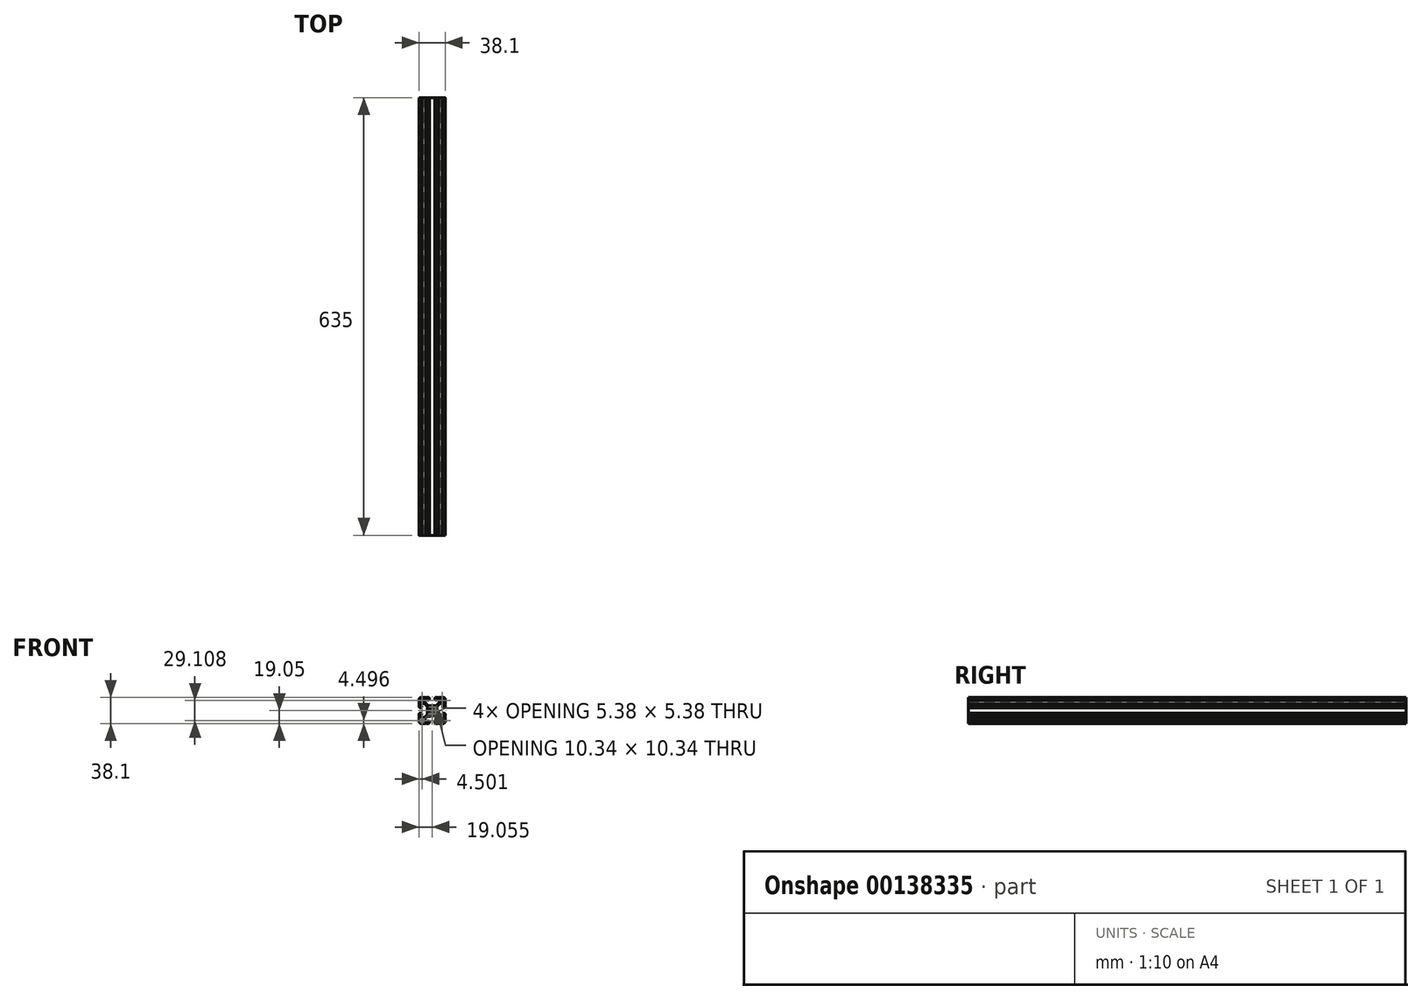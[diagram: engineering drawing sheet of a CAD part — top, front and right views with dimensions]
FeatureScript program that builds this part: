
annotation { "Feature Type Name" : "Feature", "Feature Type Description" : "" }
export const myFeature = defineFeature(function(context is Context, id is Id, definition is map)
    precondition{}
    {
        {
            var Q0;
            Q0=qCreatedBy(makeId("Front.planeOp"),FACE);
            var sketch = newSketch(context, id + "F0", { "sketchPlane" : qUnion([Q0])});
            skLineSegment(sketch, "E0", {"start": v(-126.4, 59.55) * mm, "end": v(-126.4, 54.72) * mm});
            skArc(sketch, "E1", {"start": v(-126.4, 53.2) * mm, "mid": v(-125.63, 53.96) * mm, "end": v(-126.4, 54.72) * mm});
            skArc(sketch, "E2", {"start": v(-126.4, 53.2) * mm, "mid": v(-125.47, 50.93) * mm, "end": v(-123.2, 50) * mm});
            skArc(sketch, "E3", {"start": v(-121.67, 50) * mm, "mid": v(-122.43, 50.76) * mm, "end": v(-123.2, 50) * mm});
            skLineSegment(sketch, "E4", {"start": v(-121.67, 50) * mm, "end": v(-116.84, 50) * mm});
            skArc(sketch, "E5", {"start": v(-115.32, 50) * mm, "mid": v(-116.08, 50.76) * mm, "end": v(-116.84, 50) * mm});
            skLineSegment(sketch, "E6", {"start": v(-115.32, 50) * mm, "end": v(-112.98, 50) * mm});
            skArc(sketch, "E7", {"start": v(-112.98, 50) * mm, "mid": v(-111.87, 50.46) * mm, "end": v(-111.4, 51.57) * mm});
            skLineSegment(sketch, "E8", {"start": v(-111.4, 51.57) * mm, "end": v(-111.4, 52.49) * mm});
            skArc(sketch, "E9", {"start": v(-111.4, 52.49) * mm, "mid": v(-111.87, 53.6) * mm, "end": v(-112.98, 54.06) * mm});
            skLineSegment(sketch, "E10", {"start": v(-112.98, 54.06) * mm, "end": v(-113.7, 54.06) * mm});
            skArc(sketch, "E11", {"start": v(-113.7, 54.06) * mm, "mid": v(-113.96, 53.95) * mm, "end": v(-114.08, 53.68) * mm});
            skLineSegment(sketch, "E12", {"start": v(-114.08, 53.68) * mm, "end": v(-114.08, 53.35) * mm});
            skArc(sketch, "E13", {"start": v(-114.46, 52.97) * mm, "mid": v(-114.19, 53.08) * mm, "end": v(-114.08, 53.35) * mm});
            skLineSegment(sketch, "E14", {"start": v(-114.46, 52.97) * mm, "end": v(-116.74, 52.97) * mm});
            skArc(sketch, "E15", {"start": v(-117.63, 53.86) * mm, "mid": v(-117.37, 53.23) * mm, "end": v(-116.74, 52.97) * mm});
            skLineSegment(sketch, "E16", {"start": v(-117.63, 53.86) * mm, "end": v(-117.63, 56.67) * mm});
            skArc(sketch, "E17", {"start": v(-117.26, 57.57) * mm, "mid": v(-117.54, 57.16) * mm, "end": v(-117.63, 56.67) * mm});
            skLineSegment(sketch, "E18", {"start": v(-117.26, 57.57) * mm, "end": v(-112.9, 61.93) * mm});
            skArc(sketch, "E19", {"start": v(-112, 62.3) * mm, "mid": v(-112.49, 62.2) * mm, "end": v(-112.9, 61.93) * mm});
            skLineSegment(sketch, "E20", {"start": v(-112, 62.3) * mm, "end": v(-102.7, 62.3) * mm});
            skArc(sketch, "E21", {"start": v(-101.8, 61.93) * mm, "mid": v(-102.2, 62.2) * mm, "end": v(-102.7, 62.3) * mm});
            skLineSegment(sketch, "E22", {"start": v(-101.8, 61.93) * mm, "end": v(-97.43, 57.57) * mm});
            skArc(sketch, "E23", {"start": v(-97.06, 56.67) * mm, "mid": v(-97.15, 57.16) * mm, "end": v(-97.43, 57.57) * mm});
            skLineSegment(sketch, "E24", {"start": v(-97.06, 56.67) * mm, "end": v(-97.06, 53.86) * mm});
            skArc(sketch, "E25", {"start": v(-97.95, 52.97) * mm, "mid": v(-97.32, 53.23) * mm, "end": v(-97.06, 53.86) * mm});
            skLineSegment(sketch, "E26", {"start": v(-97.95, 52.97) * mm, "end": v(-100.23, 52.97) * mm});
            skArc(sketch, "E27", {"start": v(-100.61, 53.35) * mm, "mid": v(-100.5, 53.08) * mm, "end": v(-100.23, 52.97) * mm});
            skLineSegment(sketch, "E28", {"start": v(-100.61, 53.35) * mm, "end": v(-100.61, 53.68) * mm});
            skArc(sketch, "E29", {"start": v(-100.61, 53.68) * mm, "mid": v(-100.73, 53.95) * mm, "end": v(-101, 54.06) * mm});
            skLineSegment(sketch, "E30", {"start": v(-101, 54.06) * mm, "end": v(-101.7, 54.06) * mm});
            skArc(sketch, "E31", {"start": v(-101.7, 54.06) * mm, "mid": v(-102.82, 53.6) * mm, "end": v(-103.28, 52.49) * mm});
            skLineSegment(sketch, "E32", {"start": v(-103.28, 52.49) * mm, "end": v(-103.28, 51.57) * mm});
            skArc(sketch, "E33", {"start": v(-103.28, 51.57) * mm, "mid": v(-102.82, 50.46) * mm, "end": v(-101.7, 50) * mm});
            skLineSegment(sketch, "E34", {"start": v(-101.7, 50) * mm, "end": v(-99.37, 50) * mm});
            skArc(sketch, "E35", {"start": v(-97.85, 50) * mm, "mid": v(-98.6, 50.76) * mm, "end": v(-99.37, 50) * mm});
            skLineSegment(sketch, "E36", {"start": v(-97.85, 50) * mm, "end": v(-93.02, 50) * mm});
            skArc(sketch, "E37", {"start": v(-91.5, 50) * mm, "mid": v(-92.26, 50.76) * mm, "end": v(-93.02, 50) * mm});
            skArc(sketch, "E38", {"start": v(-91.5, 50) * mm, "mid": v(-89.23, 50.93) * mm, "end": v(-88.3, 53.2) * mm});
            skArc(sketch, "E39", {"start": v(-88.3, 54.72) * mm, "mid": v(-89.06, 53.96) * mm, "end": v(-88.3, 53.2) * mm});
            skLineSegment(sketch, "E40", {"start": v(-88.3, 54.72) * mm, "end": v(-88.3, 59.55) * mm});
            skArc(sketch, "E41", {"start": v(-88.3, 61.07) * mm, "mid": v(-89.06, 60.31) * mm, "end": v(-88.3, 59.55) * mm});
            skLineSegment(sketch, "E42", {"start": v(-88.3, 61.07) * mm, "end": v(-88.3, 63.41) * mm});
            skArc(sketch, "E43", {"start": v(-88.3, 63.41) * mm, "mid": v(-88.76, 64.52) * mm, "end": v(-89.87, 64.99) * mm});
            skLineSegment(sketch, "E44", {"start": v(-89.87, 64.99) * mm, "end": v(-90.78, 64.99) * mm});
            skArc(sketch, "E45", {"start": v(-90.78, 64.99) * mm, "mid": v(-91.9, 64.52) * mm, "end": v(-92.36, 63.41) * mm});
            skLineSegment(sketch, "E46", {"start": v(-92.36, 63.41) * mm, "end": v(-92.36, 62.7) * mm});
            skArc(sketch, "E47", {"start": v(-92.36, 62.7) * mm, "mid": v(-92.25, 62.43) * mm, "end": v(-91.98, 62.32) * mm});
            skLineSegment(sketch, "E48", {"start": v(-91.98, 62.32) * mm, "end": v(-91.65, 62.32) * mm});
            skArc(sketch, "E49", {"start": v(-91.27, 61.94) * mm, "mid": v(-91.38, 62.2) * mm, "end": v(-91.65, 62.32) * mm});
            skLineSegment(sketch, "E50", {"start": v(-91.27, 61.94) * mm, "end": v(-91.27, 59.65) * mm});
            skArc(sketch, "E51", {"start": v(-92.16, 58.76) * mm, "mid": v(-91.53, 59.02) * mm, "end": v(-91.27, 59.65) * mm});
            skLineSegment(sketch, "E52", {"start": v(-92.16, 58.76) * mm, "end": v(-94.97, 58.76) * mm});
            skArc(sketch, "E53", {"start": v(-95.87, 59.13) * mm, "mid": v(-95.46, 58.86) * mm, "end": v(-94.97, 58.76) * mm});
            skLineSegment(sketch, "E54", {"start": v(-95.87, 59.13) * mm, "end": v(-100.23, 63.5) * mm});
            skArc(sketch, "E55", {"start": v(-100.6, 64.4) * mm, "mid": v(-100.5, 63.9) * mm, "end": v(-100.23, 63.5) * mm});
            skLineSegment(sketch, "E56", {"start": v(-100.6, 64.4) * mm, "end": v(-100.6, 73.7) * mm});
            skArc(sketch, "E57", {"start": v(-100.23, 74.6) * mm, "mid": v(-100.5, 74.2) * mm, "end": v(-100.6, 73.7) * mm});
            skLineSegment(sketch, "E58", {"start": v(-100.23, 74.6) * mm, "end": v(-95.87, 78.96) * mm});
            skArc(sketch, "E59", {"start": v(-94.97, 79.34) * mm, "mid": v(-95.46, 79.24) * mm, "end": v(-95.87, 78.96) * mm});
            skLineSegment(sketch, "E60", {"start": v(-94.97, 79.34) * mm, "end": v(-92.16, 79.34) * mm});
            skArc(sketch, "E61", {"start": v(-91.27, 78.45) * mm, "mid": v(-91.53, 79.08) * mm, "end": v(-92.16, 79.34) * mm});
            skLineSegment(sketch, "E62", {"start": v(-91.27, 78.45) * mm, "end": v(-91.27, 76.16) * mm});
            skArc(sketch, "E63", {"start": v(-91.65, 75.78) * mm, "mid": v(-91.38, 75.9) * mm, "end": v(-91.27, 76.16) * mm});
            skLineSegment(sketch, "E64", {"start": v(-91.65, 75.78) * mm, "end": v(-91.98, 75.78) * mm});
            skArc(sketch, "E65", {"start": v(-91.98, 75.78) * mm, "mid": v(-92.25, 75.67) * mm, "end": v(-92.36, 75.4) * mm});
            skLineSegment(sketch, "E66", {"start": v(-92.36, 75.4) * mm, "end": v(-92.36, 74.69) * mm});
            skArc(sketch, "E67", {"start": v(-92.36, 74.69) * mm, "mid": v(-91.9, 73.58) * mm, "end": v(-90.78, 73.11) * mm});
            skLineSegment(sketch, "E68", {"start": v(-90.78, 73.11) * mm, "end": v(-89.87, 73.11) * mm});
            skArc(sketch, "E69", {"start": v(-89.87, 73.11) * mm, "mid": v(-88.76, 73.58) * mm, "end": v(-88.3, 74.69) * mm});
            skLineSegment(sketch, "E70", {"start": v(-88.3, 74.69) * mm, "end": v(-88.3, 77.03) * mm});
            skArc(sketch, "E71", {"start": v(-88.3, 78.55) * mm, "mid": v(-89.06, 77.79) * mm, "end": v(-88.3, 77.03) * mm});
            skLineSegment(sketch, "E72", {"start": v(-88.3, 78.55) * mm, "end": v(-88.3, 83.38) * mm});
            skArc(sketch, "E73", {"start": v(-88.3, 84.9) * mm, "mid": v(-89.06, 84.14) * mm, "end": v(-88.3, 83.38) * mm});
            skArc(sketch, "E74", {"start": v(-88.3, 84.9) * mm, "mid": v(-89.23, 87.17) * mm, "end": v(-91.5, 88.1) * mm});
            skArc(sketch, "E75", {"start": v(-93.02, 88.1) * mm, "mid": v(-92.26, 87.34) * mm, "end": v(-91.5, 88.1) * mm});
            skLineSegment(sketch, "E76", {"start": v(-93.02, 88.1) * mm, "end": v(-97.85, 88.1) * mm});
            skArc(sketch, "E77", {"start": v(-99.37, 88.1) * mm, "mid": v(-98.6, 87.34) * mm, "end": v(-97.85, 88.1) * mm});
            skLineSegment(sketch, "E78", {"start": v(-99.37, 88.1) * mm, "end": v(-101.7, 88.1) * mm});
            skArc(sketch, "E79", {"start": v(-101.7, 88.1) * mm, "mid": v(-102.82, 87.64) * mm, "end": v(-103.28, 86.53) * mm});
            skLineSegment(sketch, "E80", {"start": v(-103.28, 86.53) * mm, "end": v(-103.28, 85.61) * mm});
            skArc(sketch, "E81", {"start": v(-103.28, 85.61) * mm, "mid": v(-102.82, 84.5) * mm, "end": v(-101.7, 84.04) * mm});
            skLineSegment(sketch, "E82", {"start": v(-101.7, 84.04) * mm, "end": v(-101, 84.04) * mm});
            skArc(sketch, "E83", {"start": v(-101, 84.04) * mm, "mid": v(-100.73, 84.15) * mm, "end": v(-100.61, 84.42) * mm});
            skLineSegment(sketch, "E84", {"start": v(-100.61, 84.42) * mm, "end": v(-100.61, 84.75) * mm});
            skArc(sketch, "E85", {"start": v(-100.23, 85.13) * mm, "mid": v(-100.5, 85.02) * mm, "end": v(-100.61, 84.75) * mm});
            skLineSegment(sketch, "E86", {"start": v(-100.23, 85.13) * mm, "end": v(-97.95, 85.13) * mm});
            skArc(sketch, "E87", {"start": v(-97.06, 84.24) * mm, "mid": v(-97.32, 84.87) * mm, "end": v(-97.95, 85.13) * mm});
            skLineSegment(sketch, "E88", {"start": v(-97.06, 84.24) * mm, "end": v(-97.06, 81.43) * mm});
            skArc(sketch, "E89", {"start": v(-97.43, 80.53) * mm, "mid": v(-97.15, 80.94) * mm, "end": v(-97.06, 81.43) * mm});
            skLineSegment(sketch, "E90", {"start": v(-97.43, 80.53) * mm, "end": v(-101.8, 76.17) * mm});
            skArc(sketch, "E91", {"start": v(-102.7, 75.8) * mm, "mid": v(-102.2, 75.9) * mm, "end": v(-101.8, 76.17) * mm});
            skLineSegment(sketch, "E92", {"start": v(-102.7, 75.8) * mm, "end": v(-112, 75.8) * mm});
            skArc(sketch, "E93", {"start": v(-112.9, 76.17) * mm, "mid": v(-112.49, 75.9) * mm, "end": v(-112, 75.8) * mm});
            skLineSegment(sketch, "E94", {"start": v(-112.9, 76.17) * mm, "end": v(-117.26, 80.53) * mm});
            skArc(sketch, "E95", {"start": v(-117.63, 81.43) * mm, "mid": v(-117.54, 80.94) * mm, "end": v(-117.26, 80.53) * mm});
            skLineSegment(sketch, "E96", {"start": v(-117.63, 81.43) * mm, "end": v(-117.63, 84.24) * mm});
            skArc(sketch, "E97", {"start": v(-116.74, 85.13) * mm, "mid": v(-117.37, 84.87) * mm, "end": v(-117.63, 84.24) * mm});
            skLineSegment(sketch, "E98", {"start": v(-116.74, 85.13) * mm, "end": v(-114.46, 85.13) * mm});
            skArc(sketch, "E99", {"start": v(-114.08, 84.75) * mm, "mid": v(-114.19, 85.02) * mm, "end": v(-114.46, 85.13) * mm});
            skLineSegment(sketch, "E100", {"start": v(-114.08, 84.75) * mm, "end": v(-114.08, 84.42) * mm});
            skArc(sketch, "E101", {"start": v(-114.08, 84.42) * mm, "mid": v(-113.96, 84.15) * mm, "end": v(-113.7, 84.04) * mm});
            skLineSegment(sketch, "E102", {"start": v(-113.7, 84.04) * mm, "end": v(-112.98, 84.04) * mm});
            skArc(sketch, "E103", {"start": v(-112.98, 84.04) * mm, "mid": v(-111.87, 84.5) * mm, "end": v(-111.4, 85.61) * mm});
            skLineSegment(sketch, "E104", {"start": v(-111.4, 85.61) * mm, "end": v(-111.4, 86.53) * mm});
            skArc(sketch, "E105", {"start": v(-111.4, 86.53) * mm, "mid": v(-111.87, 87.64) * mm, "end": v(-112.98, 88.1) * mm});
            skLineSegment(sketch, "E106", {"start": v(-112.98, 88.1) * mm, "end": v(-115.32, 88.1) * mm});
            skArc(sketch, "E107", {"start": v(-116.84, 88.1) * mm, "mid": v(-116.08, 87.34) * mm, "end": v(-115.32, 88.1) * mm});
            skLineSegment(sketch, "E108", {"start": v(-116.84, 88.1) * mm, "end": v(-121.67, 88.1) * mm});
            skArc(sketch, "E109", {"start": v(-123.2, 88.1) * mm, "mid": v(-122.43, 87.34) * mm, "end": v(-121.67, 88.1) * mm});
            skArc(sketch, "E110", {"start": v(-123.2, 88.1) * mm, "mid": v(-125.47, 87.17) * mm, "end": v(-126.4, 84.9) * mm});
            skArc(sketch, "E111", {"start": v(-126.4, 83.38) * mm, "mid": v(-125.63, 84.14) * mm, "end": v(-126.4, 84.9) * mm});
            skLineSegment(sketch, "E112", {"start": v(-126.4, 83.38) * mm, "end": v(-126.4, 78.55) * mm});
            skArc(sketch, "E113", {"start": v(-126.4, 77.03) * mm, "mid": v(-125.63, 77.79) * mm, "end": v(-126.4, 78.55) * mm});
            skLineSegment(sketch, "E114", {"start": v(-126.4, 77.03) * mm, "end": v(-126.4, 74.69) * mm});
            skArc(sketch, "E115", {"start": v(-126.4, 74.69) * mm, "mid": v(-125.93, 73.58) * mm, "end": v(-124.82, 73.11) * mm});
            skLineSegment(sketch, "E116", {"start": v(-124.82, 73.11) * mm, "end": v(-123.9, 73.11) * mm});
            skArc(sketch, "E117", {"start": v(-123.9, 73.11) * mm, "mid": v(-122.8, 73.58) * mm, "end": v(-122.33, 74.69) * mm});
            skLineSegment(sketch, "E118", {"start": v(-122.33, 74.69) * mm, "end": v(-122.33, 75.4) * mm});
            skArc(sketch, "E119", {"start": v(-122.33, 75.4) * mm, "mid": v(-122.44, 75.67) * mm, "end": v(-122.71, 75.78) * mm});
            skLineSegment(sketch, "E120", {"start": v(-122.71, 75.78) * mm, "end": v(-123.04, 75.78) * mm});
            skArc(sketch, "E121", {"start": v(-123.42, 76.16) * mm, "mid": v(-123.31, 75.9) * mm, "end": v(-123.04, 75.78) * mm});
            skLineSegment(sketch, "E122", {"start": v(-123.42, 76.16) * mm, "end": v(-123.42, 78.45) * mm});
            skArc(sketch, "E123", {"start": v(-122.53, 79.34) * mm, "mid": v(-123.16, 79.08) * mm, "end": v(-123.42, 78.45) * mm});
            skLineSegment(sketch, "E124", {"start": v(-122.53, 79.34) * mm, "end": v(-119.72, 79.34) * mm});
            skArc(sketch, "E125", {"start": v(-118.82, 78.96) * mm, "mid": v(-119.23, 79.24) * mm, "end": v(-119.72, 79.34) * mm});
            skLineSegment(sketch, "E126", {"start": v(-118.82, 78.96) * mm, "end": v(-114.46, 74.6) * mm});
            skArc(sketch, "E127", {"start": v(-114.09, 73.7) * mm, "mid": v(-114.19, 74.2) * mm, "end": v(-114.46, 74.6) * mm});
            skLineSegment(sketch, "E128", {"start": v(-114.09, 73.7) * mm, "end": v(-114.09, 64.4) * mm});
            skArc(sketch, "E129", {"start": v(-114.46, 63.5) * mm, "mid": v(-114.19, 63.9) * mm, "end": v(-114.09, 64.4) * mm});
            skLineSegment(sketch, "E130", {"start": v(-114.46, 63.5) * mm, "end": v(-118.82, 59.13) * mm});
            skArc(sketch, "E131", {"start": v(-119.72, 58.76) * mm, "mid": v(-119.23, 58.86) * mm, "end": v(-118.82, 59.13) * mm});
            skLineSegment(sketch, "E132", {"start": v(-119.72, 58.76) * mm, "end": v(-122.53, 58.76) * mm});
            skArc(sketch, "E133", {"start": v(-123.42, 59.65) * mm, "mid": v(-123.16, 59.02) * mm, "end": v(-122.53, 58.76) * mm});
            skLineSegment(sketch, "E134", {"start": v(-123.42, 59.65) * mm, "end": v(-123.42, 61.94) * mm});
            skArc(sketch, "E135", {"start": v(-123.04, 62.32) * mm, "mid": v(-123.31, 62.2) * mm, "end": v(-123.42, 61.94) * mm});
            skLineSegment(sketch, "E136", {"start": v(-123.04, 62.32) * mm, "end": v(-122.71, 62.32) * mm});
            skArc(sketch, "E137", {"start": v(-122.71, 62.32) * mm, "mid": v(-122.44, 62.43) * mm, "end": v(-122.33, 62.7) * mm});
            skLineSegment(sketch, "E138", {"start": v(-122.33, 62.7) * mm, "end": v(-122.33, 63.41) * mm});
            skArc(sketch, "E139", {"start": v(-122.33, 63.41) * mm, "mid": v(-122.8, 64.52) * mm, "end": v(-123.9, 64.99) * mm});
            skLineSegment(sketch, "E140", {"start": v(-123.9, 64.99) * mm, "end": v(-124.82, 64.99) * mm});
            skArc(sketch, "E141", {"start": v(-124.82, 64.99) * mm, "mid": v(-125.93, 64.52) * mm, "end": v(-126.4, 63.41) * mm});
            skLineSegment(sketch, "E142", {"start": v(-126.4, 63.41) * mm, "end": v(-126.4, 61.07) * mm});
            skArc(sketch, "E143", {"start": v(-95.1, 86.3) * mm, "mid": v(-95.37, 86.18) * mm, "end": v(-95.48, 85.92) * mm});
            skLineSegment(sketch, "E144", {"start": v(-92.9, 86.3) * mm, "end": v(-95.1, 86.3) * mm});
            skArc(sketch, "E145", {"start": v(-90.1, 83.5) * mm, "mid": v(-90.92, 85.48) * mm, "end": v(-92.9, 86.3) * mm});
            skLineSegment(sketch, "E146", {"start": v(-90.1, 81.3) * mm, "end": v(-90.1, 83.5) * mm});
            skArc(sketch, "E147", {"start": v(-90.48, 80.91) * mm, "mid": v(-90.21, 81.02) * mm, "end": v(-90.1, 81.3) * mm});
            skLineSegment(sketch, "E148", {"start": v(-92.25, 80.91) * mm, "end": v(-90.48, 80.91) * mm});
            skLineSegment(sketch, "E149", {"start": v(-92.8, 81.45) * mm, "end": v(-92.25, 80.91) * mm});
            skLineSegment(sketch, "E150", {"start": v(-93.33, 80.91) * mm, "end": v(-92.8, 81.45) * mm});
            skLineSegment(sketch, "E151", {"start": v(-95.1, 80.91) * mm, "end": v(-93.33, 80.91) * mm});
            skArc(sketch, "E152", {"start": v(-95.48, 81.3) * mm, "mid": v(-95.37, 81.02) * mm, "end": v(-95.1, 80.91) * mm});
            skLineSegment(sketch, "E153", {"start": v(-95.48, 83.07) * mm, "end": v(-95.48, 81.3) * mm});
            skLineSegment(sketch, "E154", {"start": v(-94.94, 83.6) * mm, "end": v(-95.48, 83.07) * mm});
            skLineSegment(sketch, "E155", {"start": v(-95.48, 84.14) * mm, "end": v(-94.94, 83.6) * mm});
            skLineSegment(sketch, "E156", {"start": v(-95.48, 56.8) * mm, "end": v(-95.48, 55.03) * mm});
            skArc(sketch, "E157", {"start": v(-95.1, 57.19) * mm, "mid": v(-95.37, 57.08) * mm, "end": v(-95.48, 56.8) * mm});
            skLineSegment(sketch, "E158", {"start": v(-93.33, 57.19) * mm, "end": v(-95.1, 57.19) * mm});
            skLineSegment(sketch, "E159", {"start": v(-92.8, 56.65) * mm, "end": v(-93.33, 57.19) * mm});
            skLineSegment(sketch, "E160", {"start": v(-92.25, 57.19) * mm, "end": v(-92.8, 56.65) * mm});
            skLineSegment(sketch, "E161", {"start": v(-90.48, 57.19) * mm, "end": v(-92.25, 57.19) * mm});
            skArc(sketch, "E162", {"start": v(-90.1, 56.8) * mm, "mid": v(-90.21, 57.08) * mm, "end": v(-90.48, 57.19) * mm});
            skLineSegment(sketch, "E163", {"start": v(-90.1, 54.6) * mm, "end": v(-90.1, 56.8) * mm});
            skArc(sketch, "E164", {"start": v(-92.9, 51.8) * mm, "mid": v(-90.92, 52.62) * mm, "end": v(-90.1, 54.6) * mm});
            skLineSegment(sketch, "E165", {"start": v(-95.1, 51.8) * mm, "end": v(-92.9, 51.8) * mm});
            skArc(sketch, "E166", {"start": v(-95.48, 52.18) * mm, "mid": v(-95.37, 51.91) * mm, "end": v(-95.1, 51.8) * mm});
            skLineSegment(sketch, "E167", {"start": v(-95.48, 53.96) * mm, "end": v(-95.48, 52.18) * mm});
            skLineSegment(sketch, "E168", {"start": v(-94.94, 54.5) * mm, "end": v(-95.48, 53.96) * mm});
            skLineSegment(sketch, "E169", {"start": v(-112.51, 65.13) * mm, "end": v(-112.51, 64.14) * mm});
            skArc(sketch, "E170", {"start": v(-112.25, 65.76) * mm, "mid": v(-112.45, 65.47) * mm, "end": v(-112.51, 65.13) * mm});
            skLineSegment(sketch, "E171", {"start": v(-110.54, 67.47) * mm, "end": v(-112.25, 65.76) * mm});
            skArc(sketch, "E172", {"start": v(-110.54, 67.47) * mm, "mid": v(-110.44, 67.66) * mm, "end": v(-110.46, 67.87) * mm});
            skArc(sketch, "E173", {"start": v(-110.46, 70.23) * mm, "mid": v(-110.67, 69.05) * mm, "end": v(-110.46, 67.87) * mm});
            skArc(sketch, "E174", {"start": v(-110.46, 70.23) * mm, "mid": v(-110.44, 70.44) * mm, "end": v(-110.54, 70.63) * mm});
            skLineSegment(sketch, "E175", {"start": v(-112.25, 72.34) * mm, "end": v(-110.54, 70.63) * mm});
            skArc(sketch, "E176", {"start": v(-112.51, 72.97) * mm, "mid": v(-112.45, 72.63) * mm, "end": v(-112.25, 72.34) * mm});
            skLineSegment(sketch, "E177", {"start": v(-112.51, 73.96) * mm, "end": v(-112.51, 72.97) * mm});
            skArc(sketch, "E178", {"start": v(-112.26, 74.22) * mm, "mid": v(-112.44, 74.14) * mm, "end": v(-112.51, 73.96) * mm});
            skLineSegment(sketch, "E179", {"start": v(-111.27, 74.22) * mm, "end": v(-112.26, 74.22) * mm});
            skArc(sketch, "E180", {"start": v(-110.64, 73.96) * mm, "mid": v(-110.93, 74.15) * mm, "end": v(-111.27, 74.22) * mm});
            skLineSegment(sketch, "E181", {"start": v(-108.93, 72.25) * mm, "end": v(-110.64, 73.96) * mm});
            skArc(sketch, "E182", {"start": v(-108.93, 72.25) * mm, "mid": v(-108.74, 72.15) * mm, "end": v(-108.52, 72.16) * mm});
            skArc(sketch, "E183", {"start": v(-106.17, 72.16) * mm, "mid": v(-107.35, 72.38) * mm, "end": v(-108.52, 72.16) * mm});
            skArc(sketch, "E184", {"start": v(-106.17, 72.16) * mm, "mid": v(-105.95, 72.15) * mm, "end": v(-105.76, 72.25) * mm});
            skLineSegment(sketch, "E185", {"start": v(-104.05, 73.96) * mm, "end": v(-105.76, 72.25) * mm});
            skArc(sketch, "E186", {"start": v(-103.42, 74.22) * mm, "mid": v(-103.76, 74.15) * mm, "end": v(-104.05, 73.96) * mm});
            skLineSegment(sketch, "E187", {"start": v(-102.43, 74.22) * mm, "end": v(-103.42, 74.22) * mm});
            skArc(sketch, "E188", {"start": v(-102.18, 73.96) * mm, "mid": v(-102.25, 74.14) * mm, "end": v(-102.43, 74.22) * mm});
            skLineSegment(sketch, "E189", {"start": v(-102.18, 72.97) * mm, "end": v(-102.18, 73.96) * mm});
            skArc(sketch, "E190", {"start": v(-102.44, 72.34) * mm, "mid": v(-102.24, 72.63) * mm, "end": v(-102.18, 72.97) * mm});
            skLineSegment(sketch, "E191", {"start": v(-104.15, 70.63) * mm, "end": v(-102.44, 72.34) * mm});
            skArc(sketch, "E192", {"start": v(-104.15, 70.63) * mm, "mid": v(-104.25, 70.44) * mm, "end": v(-104.23, 70.23) * mm});
            skArc(sketch, "E193", {"start": v(-104.23, 67.87) * mm, "mid": v(-104.02, 69.05) * mm, "end": v(-104.23, 70.23) * mm});
            skArc(sketch, "E194", {"start": v(-104.23, 67.87) * mm, "mid": v(-104.25, 67.66) * mm, "end": v(-104.15, 67.47) * mm});
            skLineSegment(sketch, "E195", {"start": v(-102.44, 65.76) * mm, "end": v(-104.15, 67.47) * mm});
            skArc(sketch, "E196", {"start": v(-102.18, 65.13) * mm, "mid": v(-102.24, 65.47) * mm, "end": v(-102.44, 65.76) * mm});
            skLineSegment(sketch, "E197", {"start": v(-102.18, 64.14) * mm, "end": v(-102.18, 65.13) * mm});
            skArc(sketch, "E198", {"start": v(-102.43, 63.88) * mm, "mid": v(-102.25, 63.96) * mm, "end": v(-102.18, 64.14) * mm});
            skLineSegment(sketch, "E199", {"start": v(-103.42, 63.88) * mm, "end": v(-102.43, 63.88) * mm});
            skArc(sketch, "E200", {"start": v(-104.05, 64.14) * mm, "mid": v(-103.76, 63.95) * mm, "end": v(-103.42, 63.88) * mm});
            skLineSegment(sketch, "E201", {"start": v(-105.76, 65.85) * mm, "end": v(-104.05, 64.14) * mm});
            skArc(sketch, "E202", {"start": v(-105.76, 65.85) * mm, "mid": v(-105.95, 65.95) * mm, "end": v(-106.17, 65.94) * mm});
            skArc(sketch, "E203", {"start": v(-108.52, 65.94) * mm, "mid": v(-107.35, 65.72) * mm, "end": v(-106.17, 65.94) * mm});
            skArc(sketch, "E204", {"start": v(-108.52, 65.94) * mm, "mid": v(-108.74, 65.95) * mm, "end": v(-108.93, 65.85) * mm});
            skLineSegment(sketch, "E205", {"start": v(-110.64, 64.14) * mm, "end": v(-108.93, 65.85) * mm});
            skArc(sketch, "E206", {"start": v(-111.27, 63.88) * mm, "mid": v(-110.93, 63.95) * mm, "end": v(-110.64, 64.14) * mm});
            skLineSegment(sketch, "E207", {"start": v(-112.26, 63.88) * mm, "end": v(-111.27, 63.88) * mm});
            skLineSegment(sketch, "E208", {"start": v(-124.6, 56.8) * mm, "end": v(-124.6, 54.6) * mm});
            skArc(sketch, "E209", {"start": v(-124.21, 57.19) * mm, "mid": v(-124.48, 57.08) * mm, "end": v(-124.6, 56.8) * mm});
            skLineSegment(sketch, "E210", {"start": v(-122.44, 57.19) * mm, "end": v(-124.21, 57.19) * mm});
            skLineSegment(sketch, "E211", {"start": v(-121.9, 56.65) * mm, "end": v(-122.44, 57.19) * mm});
            skLineSegment(sketch, "E212", {"start": v(-121.36, 57.19) * mm, "end": v(-121.9, 56.65) * mm});
            skLineSegment(sketch, "E213", {"start": v(-119.59, 57.19) * mm, "end": v(-121.36, 57.19) * mm});
            skArc(sketch, "E214", {"start": v(-119.2, 56.8) * mm, "mid": v(-119.32, 57.08) * mm, "end": v(-119.59, 57.19) * mm});
            skLineSegment(sketch, "E215", {"start": v(-119.2, 55.03) * mm, "end": v(-119.2, 56.8) * mm});
            skLineSegment(sketch, "E216", {"start": v(-119.75, 54.5) * mm, "end": v(-119.2, 55.03) * mm});
            skLineSegment(sketch, "E217", {"start": v(-119.2, 53.96) * mm, "end": v(-119.75, 54.5) * mm});
            skLineSegment(sketch, "E218", {"start": v(-119.2, 52.18) * mm, "end": v(-119.2, 53.96) * mm});
            skArc(sketch, "E219", {"start": v(-119.59, 51.8) * mm, "mid": v(-119.32, 51.91) * mm, "end": v(-119.2, 52.18) * mm});
            skLineSegment(sketch, "E220", {"start": v(-121.8, 51.8) * mm, "end": v(-119.59, 51.8) * mm});
            skLineSegment(sketch, "E221", {"start": v(-124.6, 83.5) * mm, "end": v(-124.6, 81.3) * mm});
            skArc(sketch, "E222", {"start": v(-121.8, 86.3) * mm, "mid": v(-123.77, 85.48) * mm, "end": v(-124.6, 83.5) * mm});
            skLineSegment(sketch, "E223", {"start": v(-119.59, 86.3) * mm, "end": v(-121.8, 86.3) * mm});
            skArc(sketch, "E224", {"start": v(-119.2, 85.92) * mm, "mid": v(-119.32, 86.18) * mm, "end": v(-119.59, 86.3) * mm});
            skLineSegment(sketch, "E225", {"start": v(-119.2, 84.14) * mm, "end": v(-119.2, 85.92) * mm});
            skLineSegment(sketch, "E226", {"start": v(-119.75, 83.6) * mm, "end": v(-119.2, 84.14) * mm});
            skLineSegment(sketch, "E227", {"start": v(-119.2, 83.07) * mm, "end": v(-119.75, 83.6) * mm});
            skLineSegment(sketch, "E228", {"start": v(-119.2, 81.3) * mm, "end": v(-119.2, 83.07) * mm});
            skArc(sketch, "E229", {"start": v(-119.59, 80.91) * mm, "mid": v(-119.32, 81.02) * mm, "end": v(-119.2, 81.3) * mm});
            skLineSegment(sketch, "E230", {"start": v(-121.36, 80.91) * mm, "end": v(-119.59, 80.91) * mm});
            skLineSegment(sketch, "E231", {"start": v(-121.9, 81.45) * mm, "end": v(-121.36, 80.91) * mm});
            skLineSegment(sketch, "E232", {"start": v(-122.44, 80.91) * mm, "end": v(-121.9, 81.45) * mm});
            skLineSegment(sketch, "E233", {"start": v(-124.21, 80.91) * mm, "end": v(-122.44, 80.91) * mm});
            skLineSegment(sketch, "E234", {"start": v(-95.48, 85.92) * mm, "end": v(-95.48, 84.14) * mm});
            skLineSegment(sketch, "E235", {"start": v(-95.48, 55.03) * mm, "end": v(-94.94, 54.5) * mm});
            skArc(sketch, "E236", {"start": v(-112.51, 64.14) * mm, "mid": v(-112.44, 63.96) * mm, "end": v(-112.26, 63.88) * mm});
            skArc(sketch, "E237", {"start": v(-124.6, 54.6) * mm, "mid": v(-123.77, 52.62) * mm, "end": v(-121.8, 51.8) * mm});
            skArc(sketch, "E238", {"start": v(-124.6, 81.3) * mm, "mid": v(-124.48, 81.02) * mm, "end": v(-124.21, 80.91) * mm});
            skArc(sketch, "E239", {"start": v(-126.4, 59.55) * mm, "mid": v(-125.63, 60.31) * mm, "end": v(-126.4, 61.07) * mm});
            skSolve(sketch);
        }
        {
            var Q0;
            Q0=makeQuery(id+"F0.imprint","IMPRINT",FACE,{"disambiguationData":[TD([[makeQuery(id+"F0.imprint","IMPRINT",EDGE,{"derivedFrom":sQuery(id+"F0.wireOp",EDGE,"E0")}),1.0]])]});
            extrude(context, id + "F1", {"entities" : qUnion([Q0]), "endBound" : BoundingType.SYMMETRIC, "depth" : 635 * mm});
        }
    });
